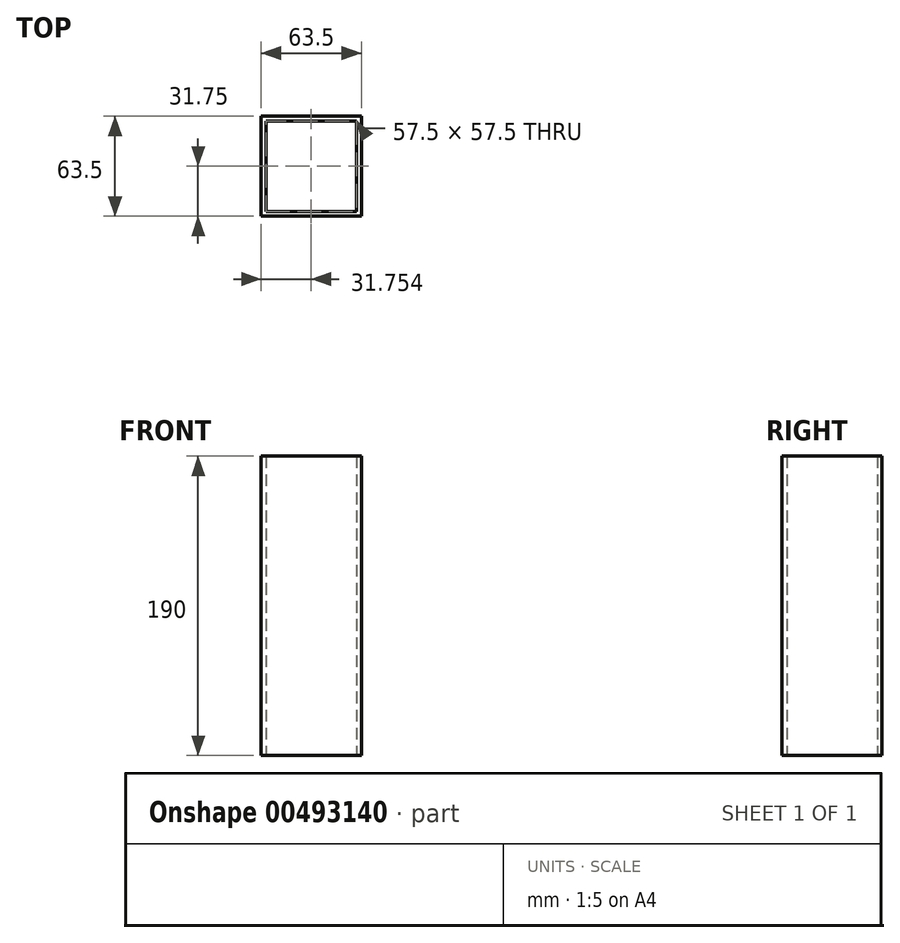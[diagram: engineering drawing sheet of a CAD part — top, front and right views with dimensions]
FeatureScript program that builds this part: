
annotation { "Feature Type Name" : "Feature", "Feature Type Description" : "" }
export const myFeature = defineFeature(function(context is Context, id is Id, definition is map)
    precondition{}
    {
        {
            var Q0;
            Q0=qCreatedBy(makeId("Top.planeOp"),FACE);
            var sketch = newSketch(context, id + "F0", { "sketchPlane" : qUnion([Q0])});
            skLineSegment(sketch, "E0.bottom", {"start": v(-85.74, 19.43) * mm, "end": v(-28.24, 19.43) * mm});
            skLineSegment(sketch, "E0.top", {"start": v(-85.74, -38.07) * mm, "end": v(-28.24, -38.07) * mm});
            skLineSegment(sketch, "E0.left", {"start": v(-85.74, 19.43) * mm, "end": v(-85.74, -38.07) * mm});
            skLineSegment(sketch, "E0.right", {"start": v(-28.24, 19.43) * mm, "end": v(-28.24, -38.07) * mm});
            skLineSegment(sketch, "E1.bottom", {"start": v(-88.74, 22.43) * mm, "end": v(-25.24, 22.43) * mm});
            skLineSegment(sketch, "E1.top", {"start": v(-88.74, -41.07) * mm, "end": v(-25.24, -41.07) * mm});
            skLineSegment(sketch, "E1.left", {"start": v(-88.74, 22.43) * mm, "end": v(-88.74, -41.07) * mm});
            skLineSegment(sketch, "E1.right", {"start": v(-25.24, 22.43) * mm, "end": v(-25.24, -41.07) * mm});
            skSolve(sketch);
        }
        {
            var Q0;
            Q0 = qSketchRegion(id + "F0", true);
            extrude(context, id + "F1", {"entities" : qUnion([Q0]), "depth" : 190 * mm});
        }
    });
